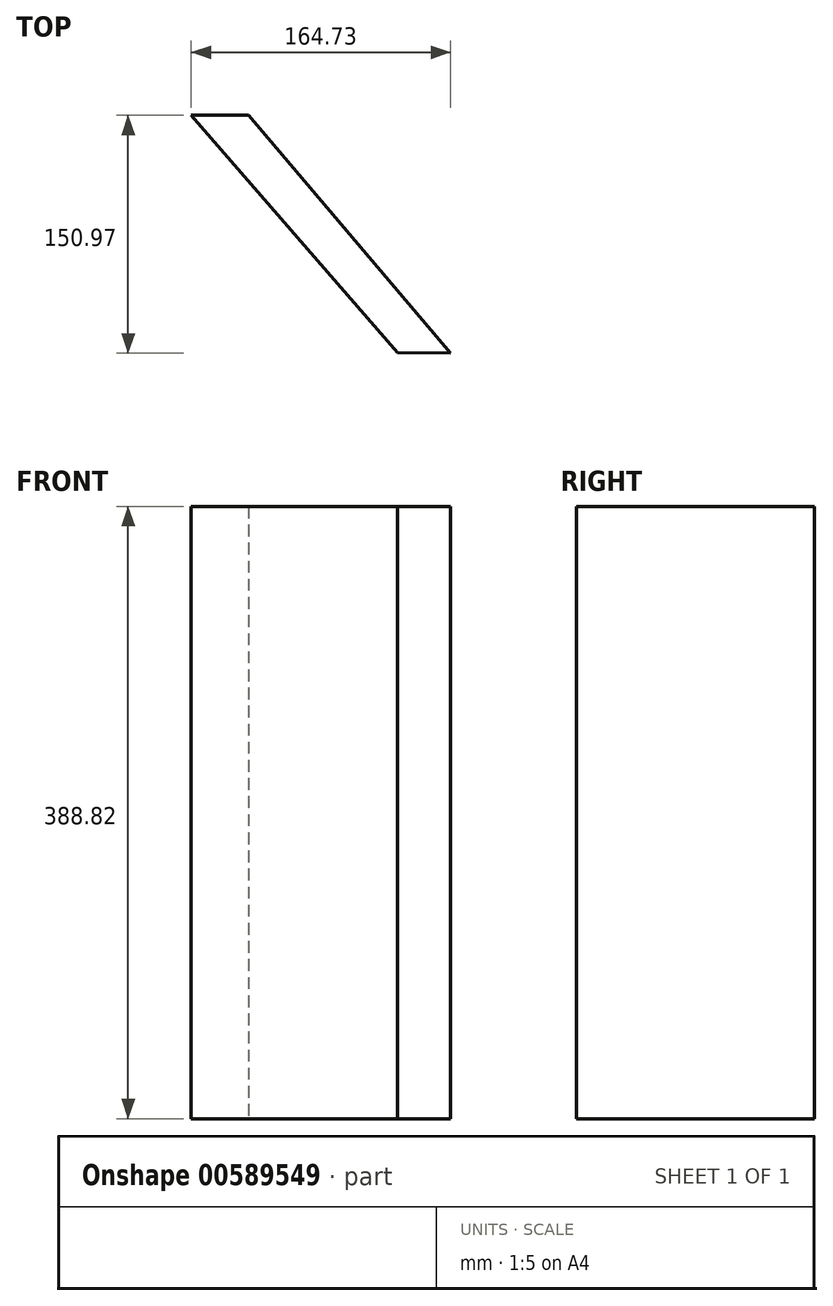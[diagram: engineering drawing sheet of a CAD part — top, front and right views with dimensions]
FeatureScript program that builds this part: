
annotation { "Feature Type Name" : "Feature", "Feature Type Description" : "" }
export const myFeature = defineFeature(function(context is Context, id is Id, definition is map)
    precondition{}
    {
        {
            var Q0;
            Q0=qCreatedBy(makeId("Top.planeOp"),FACE);
            var sketch = newSketch(context, id + "F0", { "sketchPlane" : qUnion([Q0])});
            skLineSegment(sketch, "E0", {"start": v(33.65, 0) * mm, "end": v(0, 0) * mm});
            skLineSegment(sketch, "E1", {"start": v(0, 0) * mm, "end": v(33.7, -0.18) * mm});
            skLineSegment(sketch, "E2", {"start": v(33.7, -0.18) * mm, "end": v(-94.66, 150.79) * mm});
            skLineSegment(sketch, "E3", {"start": v(-94.66, 150.79) * mm, "end": v(-131.03, 150.79) * mm});
            skLineSegment(sketch, "E4", {"start": v(-131.03, 150.79) * mm, "end": v(0, 0) * mm});
            skSolve(sketch);
        }
        {
            var Q0;
            {var subQ0=sQuery(id+"F0.wireOp",EDGE,"E1");Q0=makeQuery(id+"F0.imprint","IMPRINT",FACE,{"disambiguationData":[TD([[makeQuery(id+"F0.imprint","IMPRINT",EDGE,{"derivedFrom":subQ0}),1.0]])]});}
            var Q1;
            {var subQ4=sQuery(id+"F0.wireOp",EDGE,"E3");Q1=makeQuery(id+"F0.imprint","IMPRINT",FACE,{"disambiguationData":[TD([[makeQuery(id+"F0.imprint","IMPRINT",EDGE,{"derivedFrom":subQ4}),1.0]])]});}
            extrude(context, id + "F1", {"entities" : qUnion([Q0, Q1]), "depth" : 388.82 * mm, "offsetDistance" : 25.4 * mm});
        }
    });
